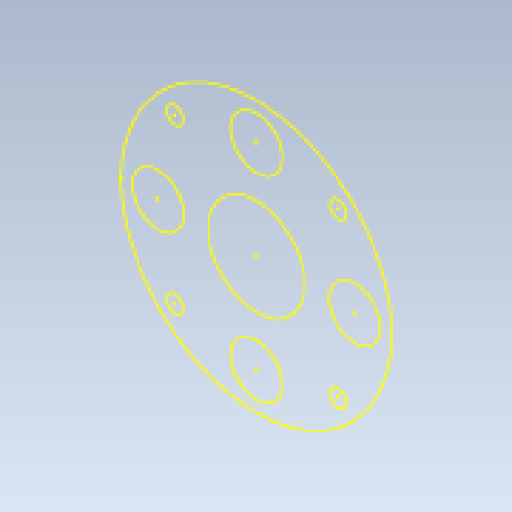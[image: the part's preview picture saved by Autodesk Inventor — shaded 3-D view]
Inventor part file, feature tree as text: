
AUTODESK INVENTOR PART (.ipt)
format: ipt  version: 2023 (Build 270158000, 158)  size: 91,648 bytes
history: native  units: in
note: dims shown in document units (in); Inventor stores cm internally (conversion verified against a paired STEP export)
features: other x3, sketch x2, reference x2, plane x1
ambient origin geometry x8: Origin, YZ Plane, XZ Plane, XY Plane, X Axis, Y Axis, Z Axis, Center Point
feature tree (8):
  sketch  "Sketch1"  dims[d0=0.25in]
  plane  "Work Plane1"
  sketch  "Sketch2"  dims[d1=0.25in d2=0.25in]
  reference  "Reference1"
  reference  "Reference2"
  other  "Gearbox Assembly.iam"
  other  "Drive Motor:1"
  other  "CH-1-02-RearGearboxHousingMotorSide:1"
